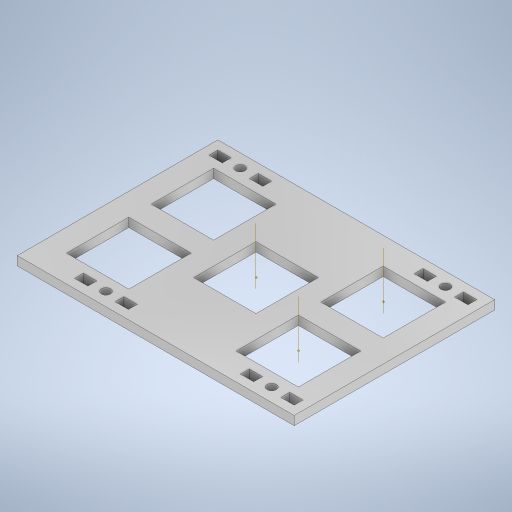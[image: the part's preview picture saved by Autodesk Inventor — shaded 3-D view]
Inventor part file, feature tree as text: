
AUTODESK INVENTOR PART (.ipt)
format: ipt  version: 2024.1 (Build 281209000, 209)  size: 833,536 bytes
history: native  units: mm
features: other x18, extrude x1, sketch x1
ambient origin geometry x8: Origin, YZ Plane, XZ Plane, XY Plane, X Axis, Y Axis, Z Axis, Center Point
bodies: Body1 (feature_tree)
feature tree (20):
  other  "shared_parameters.ipt"
  other  "Blocs"
  extrude  "Base"  Depth=2.0mm TaperAngle=0.0deg
  other  "Point de construction9"
  other  "Point de construction10"
  other  "Point de construction11"
  other  "Axe de construction9"
  other  "Axe de construction10"
  other  "Axe de construction11"
  sketch  "Esquisse2"
  other  "screw_anchor"
  other  "anchor"
  other  "Anchor (screw side)"
  other  "Anchor (nut side)"
  other  "Screwless anchor (male)"
  other  "Screwless anchor (female)"
  other  "Anchor (screw side):1"
  other  "Anchor (screw side):2"
  other  "Anchor (screw side):3"
  other  "Anchor (screw side):4"
